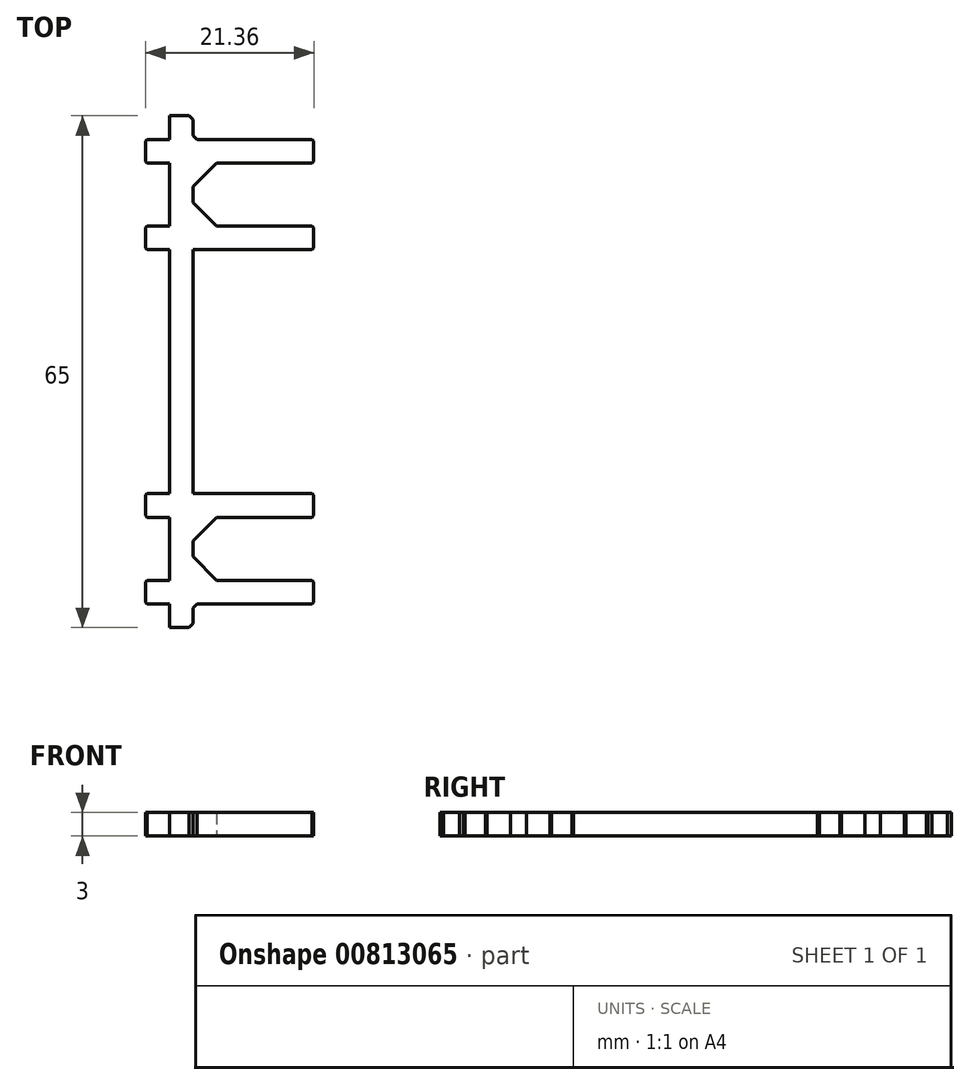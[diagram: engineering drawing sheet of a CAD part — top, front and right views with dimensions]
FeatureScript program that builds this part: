
annotation { "Feature Type Name" : "Feature", "Feature Type Description" : "" }
export const myFeature = defineFeature(function(context is Context, id is Id, definition is map)
    precondition{}
    {
        {
            var Q0;
            Q0=qCreatedBy(makeId("Top.planeOp"),FACE);
            var sketch = newSketch(context, id + "F0", { "sketchPlane" : qUnion([Q0])});
            skLineSegment(sketch, "E0", {"start": v(-1.68, 26.5) * mm, "end": v(-4.67, 23.5) * mm});
            skLineSegment(sketch, "E1", {"start": v(-4.68, 21.5) * mm, "end": v(-1.68, 18.5) * mm});
            skLineSegment(sketch, "E2", {"start": v(-1.68, -18.5) * mm, "end": v(-4.68, -21.5) * mm});
            skLineSegment(sketch, "E3", {"start": v(-4.68, -23.5) * mm, "end": v(-1.68, -26.5) * mm});
            skLineSegment(sketch, "E4", {"start": v(-4.68, 23.5) * mm, "end": v(-4.68, 21.5) * mm});
            skLineSegment(sketch, "E5", {"start": v(-4.68, -21.5) * mm, "end": v(-4.68, -23.5) * mm});
            skLineSegment(sketch, "E6", {"start": v(-7.68, 26.5) * mm, "end": v(-7.68, 18.5) * mm});
            skLineSegment(sketch, "E7", {"start": v(-7.68, 15.5) * mm, "end": v(-7.68, -15.5) * mm});
            skLineSegment(sketch, "E8", {"start": v(-7.68, -18.5) * mm, "end": v(-7.68, -26.5) * mm});
            skLineSegment(sketch, "E9", {"start": v(-7.68, 29.5) * mm, "end": v(-7.68, 32.5) * mm});
            skLineSegment(sketch, "E10", {"start": v(-7.68, -29.5) * mm, "end": v(-7.68, -32.5) * mm});
            skLineSegment(sketch, "E11", {"start": v(-4.68, 15.5) * mm, "end": v(-4.68, -15.5) * mm});
            skLineSegment(sketch, "E12", {"start": v(-7.68, 32.5) * mm, "end": v(-5.17, 32.5) * mm});
            skLineSegment(sketch, "E13", {"start": v(-4.68, 32) * mm, "end": v(-5.17, 32.5) * mm});
            skLineSegment(sketch, "E14", {"start": v(-7.68, -32.5) * mm, "end": v(-5.17, -32.5) * mm});
            skLineSegment(sketch, "E15", {"start": v(-5.17, -32.5) * mm, "end": v(-4.68, -32) * mm});
            skLineSegment(sketch, "E16", {"start": v(-4.68, 32) * mm, "end": v(-4.68, 30) * mm});
            skLineSegment(sketch, "E17", {"start": v(-4.68, 30) * mm, "end": v(-4.17, 29.5) * mm});
            skLineSegment(sketch, "E18", {"start": v(-4.68, -30) * mm, "end": v(-4.68, -32) * mm});
            skLineSegment(sketch, "E19", {"start": v(-4.68, -30) * mm, "end": v(-4.17, -29.5) * mm});
            skLineSegment(sketch, "E20", {"start": v(-4.17, 29.5) * mm, "end": v(10.47, 29.5) * mm});
            skLineSegment(sketch, "E21", {"start": v(10.47, 29.5) * mm, "end": v(10.68, 29.3) * mm});
            skLineSegment(sketch, "E22", {"start": v(10.68, 29.3) * mm, "end": v(10.68, 26.7) * mm});
            skLineSegment(sketch, "E23", {"start": v(-1.68, 26.5) * mm, "end": v(10.47, 26.5) * mm});
            skLineSegment(sketch, "E24", {"start": v(10.68, 26.7) * mm, "end": v(10.47, 26.5) * mm});
            skLineSegment(sketch, "E25", {"start": v(-1.68, 18.5) * mm, "end": v(10.47, 18.5) * mm});
            skLineSegment(sketch, "E26", {"start": v(10.47, 18.5) * mm, "end": v(10.68, 18.3) * mm});
            skLineSegment(sketch, "E27", {"start": v(10.68, 18.3) * mm, "end": v(10.68, 15.7) * mm});
            skLineSegment(sketch, "E28", {"start": v(10.47, 15.5) * mm, "end": v(-4.68, 15.5) * mm});
            skLineSegment(sketch, "E29", {"start": v(10.68, 15.7) * mm, "end": v(10.47, 15.5) * mm});
            skLineSegment(sketch, "E30", {"start": v(10.47, -15.5) * mm, "end": v(-4.68, -15.5) * mm});
            skLineSegment(sketch, "E31", {"start": v(10.47, -15.5) * mm, "end": v(10.68, -15.7) * mm});
            skLineSegment(sketch, "E32", {"start": v(10.68, -15.7) * mm, "end": v(10.68, -18.3) * mm});
            skLineSegment(sketch, "E33", {"start": v(-1.68, -18.5) * mm, "end": v(10.47, -18.5) * mm});
            skLineSegment(sketch, "E34", {"start": v(10.68, -18.3) * mm, "end": v(10.47, -18.5) * mm});
            skLineSegment(sketch, "E35", {"start": v(10.47, -26.5) * mm, "end": v(-1.67, -26.5) * mm});
            skLineSegment(sketch, "E36", {"start": v(10.47, -26.5) * mm, "end": v(10.68, -26.7) * mm});
            skLineSegment(sketch, "E37", {"start": v(10.68, -26.7) * mm, "end": v(10.68, -29.3) * mm});
            skLineSegment(sketch, "E38", {"start": v(-4.17, -29.5) * mm, "end": v(10.47, -29.5) * mm});
            skLineSegment(sketch, "E39", {"start": v(10.68, -29.3) * mm, "end": v(10.47, -29.5) * mm});
            skLineSegment(sketch, "E40", {"start": v(-10.47, 29.5) * mm, "end": v(-7.68, 29.5) * mm});
            skLineSegment(sketch, "E41", {"start": v(-10.47, 29.5) * mm, "end": v(-10.67, 29.3) * mm});
            skLineSegment(sketch, "E42", {"start": v(-10.67, 29.3) * mm, "end": v(-10.67, 26.7) * mm});
            skLineSegment(sketch, "E43", {"start": v(-10.47, 26.5) * mm, "end": v(-7.68, 26.5) * mm});
            skLineSegment(sketch, "E44", {"start": v(-10.67, 26.7) * mm, "end": v(-10.47, 26.5) * mm});
            skLineSegment(sketch, "E45", {"start": v(-7.68, 18.5) * mm, "end": v(-10.47, 18.5) * mm});
            skLineSegment(sketch, "E46", {"start": v(-10.47, 18.5) * mm, "end": v(-10.67, 18.3) * mm});
            skLineSegment(sketch, "E47", {"start": v(-10.67, 18.3) * mm, "end": v(-10.67, 15.7) * mm});
            skLineSegment(sketch, "E48", {"start": v(-10.47, 15.5) * mm, "end": v(-7.68, 15.5) * mm});
            skLineSegment(sketch, "E49", {"start": v(-10.67, 15.7) * mm, "end": v(-10.47, 15.5) * mm});
            skLineSegment(sketch, "E50", {"start": v(-7.68, -15.5) * mm, "end": v(-10.47, -15.5) * mm});
            skLineSegment(sketch, "E51", {"start": v(-10.47, -15.5) * mm, "end": v(-10.67, -15.7) * mm});
            skLineSegment(sketch, "E52", {"start": v(-10.67, -15.7) * mm, "end": v(-10.67, -18.3) * mm});
            skLineSegment(sketch, "E53", {"start": v(-10.47, -18.5) * mm, "end": v(-7.68, -18.5) * mm});
            skLineSegment(sketch, "E54", {"start": v(-10.67, -18.3) * mm, "end": v(-10.47, -18.5) * mm});
            skLineSegment(sketch, "E55", {"start": v(-7.68, -26.5) * mm, "end": v(-10.47, -26.5) * mm});
            skLineSegment(sketch, "E56", {"start": v(-10.47, -26.5) * mm, "end": v(-10.67, -26.7) * mm});
            skLineSegment(sketch, "E57", {"start": v(-10.67, -26.7) * mm, "end": v(-10.67, -29.3) * mm});
            skLineSegment(sketch, "E58", {"start": v(-10.47, -29.5) * mm, "end": v(-7.68, -29.5) * mm});
            skLineSegment(sketch, "E59", {"start": v(-10.67, -29.3) * mm, "end": v(-10.47, -29.5) * mm});
            skSolve(sketch);
        }
        {
            var Q0;
            Q0=qSketchRegion(id+"F0",true);
            extrude(context, id + "F1", {"entities" : qUnion([Q0]), "depth" : 3 * mm, "offsetDistance" : 25 * mm});
        }
    });
